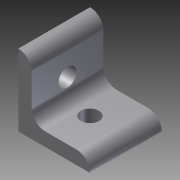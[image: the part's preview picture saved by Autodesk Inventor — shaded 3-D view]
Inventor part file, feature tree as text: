
AUTODESK INVENTOR PART (.ipt)
format: ipt  version: 2012 (Build 160160000, 160)  size: 104,960 bytes
history: native  units: in
note: dims shown in document units (in); Inventor stores cm internally (conversion verified against a paired STEP export)
features: extrude x3, sketch x3
ambient origin geometry x8: Origin, YZ Plane, XZ Plane, XY Plane, X Axis, Y Axis, Z Axis, Center Point
bodies: Solid1 (feature_tree)
feature tree (6):
  extrude  "Extrusion1"  Depth=1.0in
  extrude  "Extrusion2"  Depth=0.1875in
  extrude  "Extrusion3"  Depth=0.25in
  sketch  "Sketch1"  dims[d0=1.0in d1=1.0in]
  sketch  "Sketch2"  dims[d2=0.1875in d3=0.1875in]
  sketch  "Sketch3"  dims[d4=1.0in d5=0.0in d6=0.25in d7=0.5in d8=0.5in d9=1.0in d10=0.0in d11=0.25in d14=1.0in d15=0.0in]
